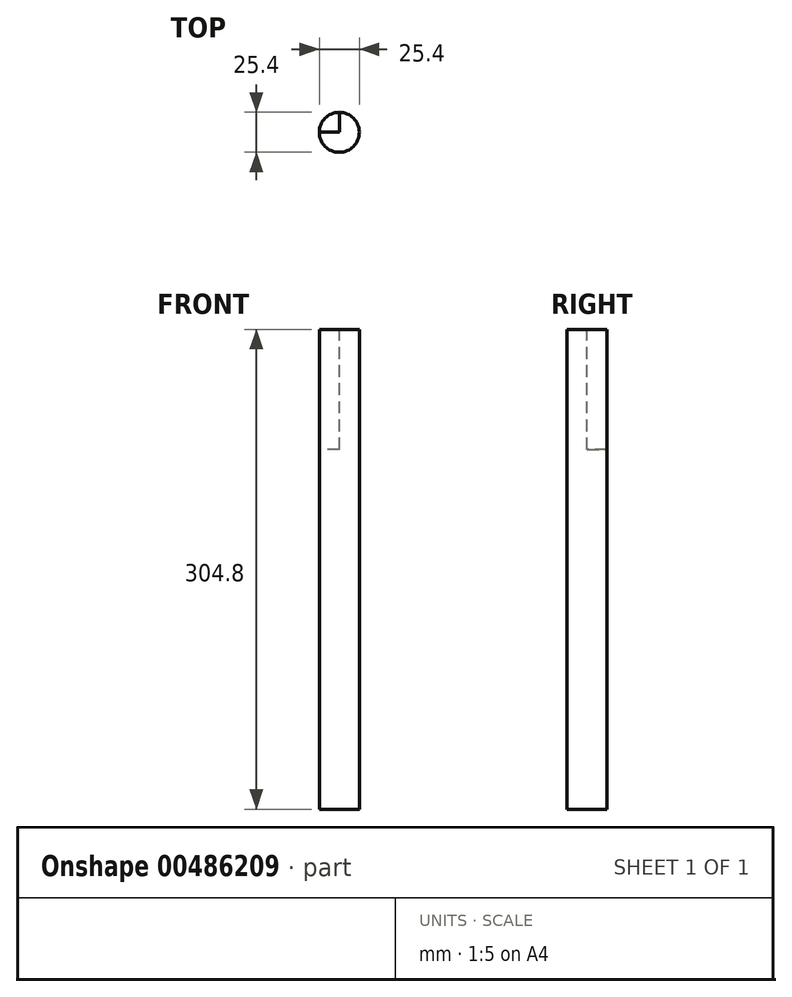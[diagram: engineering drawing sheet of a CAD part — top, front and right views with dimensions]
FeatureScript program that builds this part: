
annotation { "Feature Type Name" : "Feature", "Feature Type Description" : "" }
export const myFeature = defineFeature(function(context is Context, id is Id, definition is map)
    precondition{}
    {
        {
            var Q0;
            Q0=qCreatedBy(makeId("Top.planeOp"),FACE);
            var sketch = newSketch(context, id + "F0", { "sketchPlane" : qUnion([Q0])});
            skCircle(sketch, "E0", {"center": v(-10.88, 9.93) * mm, "radius": 12.7 * mm});
            skSolve(sketch);
        }
        {
            var Q0;
            Q0=makeQuery(id+"F0.imprint","IMPRINT",FACE,{"disambiguationData":[TD([[makeQuery(id+"F0.imprint","IMPRINT",EDGE,{"derivedFrom":sQuery(id+"F0.wireOp",EDGE,"E0")}),1.0]])]});
            extrude(context, id + "F1", {"entities" : qUnion([Q0]), "depth" : 304.8 * mm, "offsetDistance" : 25.4 * mm});
        }
        {
            var Q0;
            Q0=makeQuery(id+"F1.opExtrude","CAP_FACE",FACE,{"disambiguationData":[OSD([sQuery(id+"F0.wireOp",EDGE,"E0")])],"isStart":false});
            var sketch = newSketch(context, id + "F2", { "sketchPlane" : qUnion([Q0])});
            skLineSegment(sketch, "E1", {"start": v(1.41, 13.1) * mm, "end": v(-4.94, 13.1) * mm});
            skLineSegment(sketch, "E2", {"start": v(-4.94, 13.1) * mm, "end": v(-4.94, 6.75) * mm});
            skLineSegment(sketch, "E3", {"start": v(-4.94, 6.75) * mm, "end": v(1.41, 6.75) * mm});
            skSolve(sketch);
        }
        {
            var Q0;
            {var subQ0=sQuery(id+"F2.wireOp",EDGE,"E1");Q0=makeQuery(id+"F2.imprint","IMPRINT",FACE,{"disambiguationData":[TD([[makeQuery(id+"F2.imprint","IMPRINT",EDGE,{"derivedFrom":subQ0}),1.0]])]});}
            extrude(context, id + "F3", {"entities" : qUnion([Q0]), "operationType" : NewBodyOperationType.REMOVE, "depth" : 76.2 * mm, "offsetDistance" : 25.4 * mm});
        }
        {
            var Q0;
            Q0=makeQuery(id+"F1.opExtrude","CAP_FACE",FACE,{"disambiguationData":[OSD([sQuery(id+"F0.wireOp",EDGE,"E0")])],"isStart":false});
            var sketch = newSketch(context, id + "F4", { "sketchPlane" : qUnion([Q0])});
            skLineSegment(sketch, "E4", {"start": v(-10.88, 9.93) * mm, "end": v(-23.58, 9.93) * mm, "construction": true});
            skLineSegment(sketch, "E5", {"start": v(-23.58, 9.93) * mm, "end": v(-10.88, 9.93) * mm, "construction": true});
            skLineSegment(sketch, "E6", {"start": v(-10.88, 9.93) * mm, "end": v(-23.58, 9.93) * mm});
            skLineSegment(sketch, "E7", {"start": v(-10.88, 9.93) * mm, "end": v(-10.88, 22.63) * mm});
            skSolve(sketch);
        }
        {
            var Q0;
            {var subQ0=sQuery(id+"F4.wireOp",EDGE,"E6");Q0=makeQuery(id+"F4.imprint","IMPRINT",FACE,{"disambiguationData":[TD([[makeQuery(id+"F4.imprint","IMPRINT",EDGE,{"derivedFrom":subQ0}),-1.0]])]});}
            extrude(context, id + "F5", {"entities" : qUnion([Q0]), "operationType" : NewBodyOperationType.REMOVE, "oppositeDirection" : true, "depth" : 76.2 * mm, "offsetDistance" : 25.4 * mm});
        }
    });
